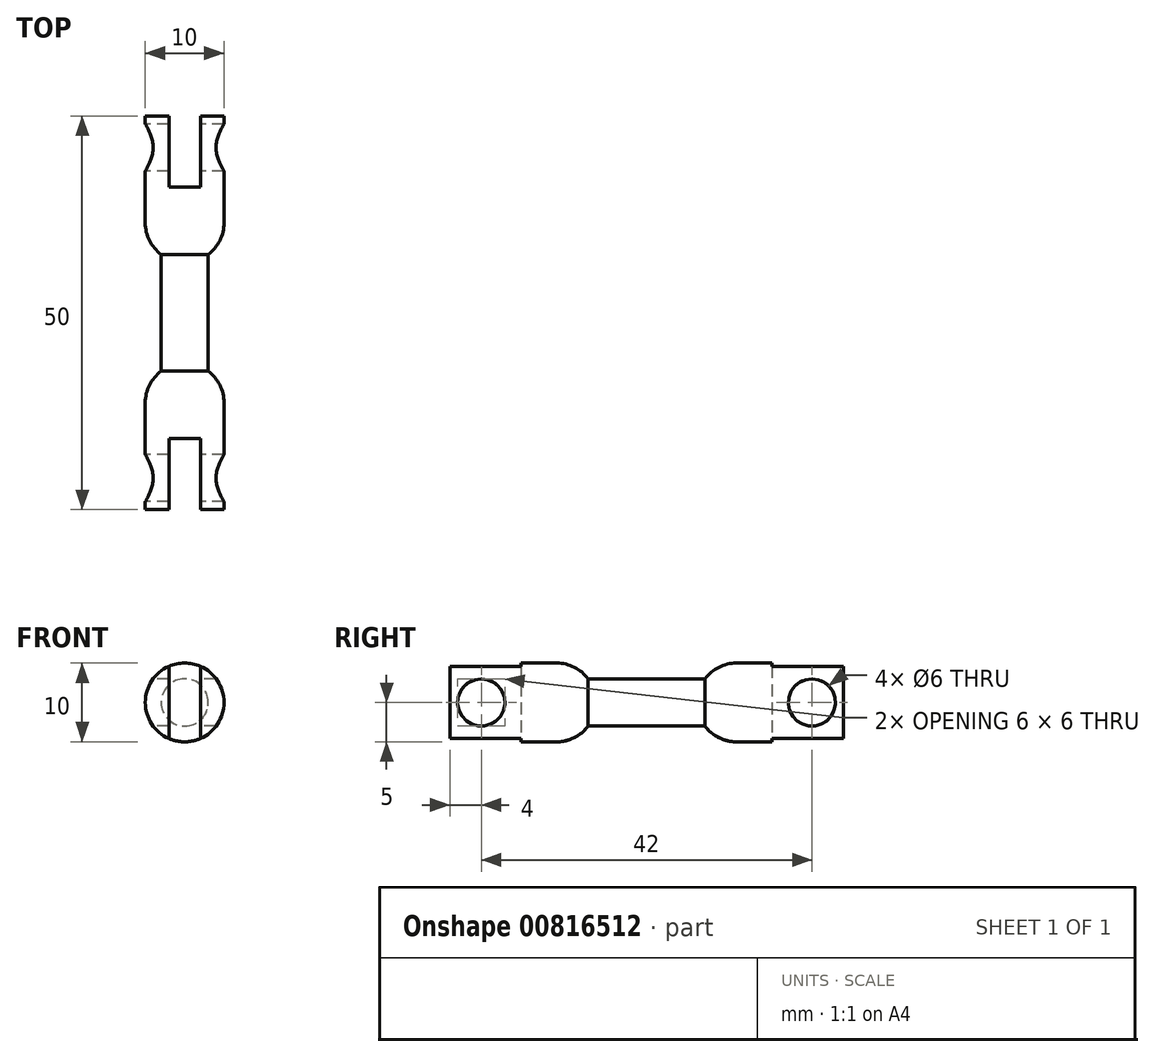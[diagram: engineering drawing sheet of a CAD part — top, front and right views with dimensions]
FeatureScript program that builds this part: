
annotation { "Feature Type Name" : "Feature", "Feature Type Description" : "" }
export const myFeature = defineFeature(function(context is Context, id is Id, definition is map)
    precondition{}
    {
        {
            assignVariable(context, id + "F0", {"name" : "Bolzenlaenge", "anyValue" : 15});
        }
        {
            var Q0;
            Q0=qCreatedBy(makeId("Front.planeOp"),FACE);
            var sketch = newSketch(context, id + "F1", { "sketchPlane" : qUnion([Q0])});
            skCircle(sketch, "E0", {"center": v(0, 0) * mm, "radius": 3 * mm});
            skCircle(sketch, "E1", {"center": v(0, 0) * mm, "radius": 5 * mm});
            skSolve(sketch);
        }
        {
            var Q0;
            Q0=makeQuery(id+"F1.imprint","IMPRINT",FACE,{"disambiguationData":[TD([[makeQuery(id+"F1.imprint","IMPRINT",EDGE,{"derivedFrom":sQuery(id+"F1.wireOp",EDGE,"E0")}),1.0]])]});
            var Q1;
            Q1=sQuery(id+"F1.wireOp",EDGE,"E0");
            extrude(context, id + "F2", {"entities" : qUnion([Q0]), "surfaceEntities" : qUnion([Q1]), "depth" : (getVariable(context, 'Bolzenlaenge')) * mm, "offsetDistance" : 25 * mm});
        }
        {
            var Q0;
            Q0=makeQuery(id+"F1.imprint","IMPRINT",FACE,{"disambiguationData":[TD([[makeQuery(id+"F1.imprint","IMPRINT",EDGE,{"derivedFrom":sQuery(id+"F1.wireOp",EDGE,"E0")}),-1.0]])]});
            var Q1;
            Q1=makeQuery(id+"F1.imprint","IMPRINT",FACE,{"disambiguationData":[TD([[makeQuery(id+"F1.imprint","IMPRINT",EDGE,{"derivedFrom":sQuery(id+"F1.wireOp",EDGE,"E0")}),1.0]])]});
            extrude(context, id + "F3", {"entities" : qUnion([Q0, Q1]), "oppositeDirection" : true, "depth" : 10 * mm, "offsetDistance" : 25 * mm, "hasSecondDirection" : true, "secondDirectionOppositeDirection" : false, "secondDirectionDepth" : 8.58 * mm});
        }
        {
            var Q0;
            Q0=makeQuery(id+"F3.opExtrude","CAP_EDGE",EDGE,{"disambiguationData":[OSD([sQuery(id+"F1.wireOp",EDGE,"E1")])],"isStart":true});
            fillet(context, id + "F4", {"entities" : qUnion([Q0]), "radius" : 5 * mm, "tangentPropagation" : true, "allowEdgeOverflow" : false});
        }
        {
            var Q0;
            Q0=makeQuery(id+"F3.opExtrude","CAP_FACE",FACE,{"disambiguationData":[OSD([sQuery(id+"F1.wireOp",EDGE,"E1")])],"isStart":false});
            var sketch = newSketch(context, id + "F5", { "sketchPlane" : qUnion([Q0])});
            skArc(sketch, "E2", {"start": v(-2, -4.58) * mm, "mid": v(0, -5) * mm, "end": v(2, -4.58) * mm});
            skLineSegment(sketch, "E3", {"start": v(-2, 4.58) * mm, "end": v(-2, -4.58) * mm});
            skLineSegment(sketch, "E4.MirrorCS", {"start": v(2, 4.58) * mm, "end": v(2, -4.58) * mm});
            skPoint(sketch, "E5.orphan", {"position": v(-2, 5.32) * mm});
            skPoint(sketch, "E6.orphan", {"position": v(-2, -6.45) * mm});
            skPoint(sketch, "E7.orphan", {"position": v(2, -6.45) * mm});
            skArc(sketch, "E8.trimOffspring", {"start": v(2, 4.58) * mm, "mid": v(0, 5) * mm, "end": v(-2, 4.58) * mm});
            skPoint(sketch, "E9.orphan", {"position": v(2, 5.32) * mm});
            skSolve(sketch);
        }
        {
            var Q0;
            Q0=makeQuery(id+"F5.imprint","IMPRINT",FACE,{"disambiguationData":[TD([[makeQuery(id+"F5.imprint","IMPRINT",EDGE,{"derivedFrom":sQuery(id+"F5.wireOp",EDGE,"E2")}),-1.0]])]});
            extrude(context, id + "F6", {"entities" : qUnion([Q0]), "operationType" : NewBodyOperationType.REMOVE, "oppositeDirection" : true, "depth" : 9.05 * mm, "offsetDistance" : 25 * mm});
        }
        {
            var Q0;
            Q0=makeQuery(id+"F6.boolean.opBoolean","COPY",FACE,{"derivedFrom":makeQuery(id+"F6.opExtrude","SWEPT_FACE",FACE,{"disambiguationData":[OSD([sQuery(id+"F5.wireOp",EDGE,"E4.MirrorCS")])]})});
            var sketch = newSketch(context, id + "F7", { "sketchPlane" : qUnion([Q0])});
            skCircle(sketch, "E10", {"center": v(6, 0) * mm, "radius": 3 * mm});
            skSolve(sketch);
        }
        {
            var Q0;
            {var subQ0=sQuery(id+"F7.wireOp",EDGE,"E10");var subQ1=makeQuery(id+"F6.boolean.opBoolean","COPY",EDGE,{"derivedFrom":makeQuery(id+"F6.opExtrude","CAP_EDGE",EDGE,{"disambiguationData":[OSD([sQuery(id+"F5.wireOp",EDGE,"E4.MirrorCS")])],"isStart":false})});var subQ2=makeQuery(id+"F7.imprint","INTERSECT",VERTEX,{"disambiguationData":[OD(0.0)],"derivedFrom":[subQ1,subQ0]});Q0=makeQuery(id+"F7.imprint","IMPRINT",FACE,{"disambiguationData":[TD([[makeQuery(id+"F7.imprint","IMPRINT",EDGE,{"disambiguationData":[TD([[subQ2,-1.0]])],"derivedFrom":subQ0}),1.0]])]});}
            extrude(context, id + "F8", {"entities" : qUnion([Q0]), "operationType" : NewBodyOperationType.REMOVE, "depth" : 25 * mm, "offsetDistance" : 25 * mm, "hasSecondDirection" : true, "secondDirectionOppositeDirection" : true, "secondDirectionDepth" : 25 * mm});
        }
        {
            var Q0;
            Q0=makeQuery(id+"F2.opExtrude","SWEPT_BODY",BODY,{"disambiguationData":[OSD([sQuery(id+"F1.wireOp",EDGE,"E0")])]});
            var Q1;
            Q1=makeQuery(id+"F3.opExtrude","SWEPT_BODY",BODY,{"disambiguationData":[OSD([sQuery(id+"F1.wireOp",EDGE,"E1")])]});
            var Q2;
            Q2=makeQuery(id+"F2.opExtrude","CAP_FACE",FACE,{"disambiguationData":[OSD([sQuery(id+"F1.wireOp",EDGE,"E0")])],"isStart":false});
            mirror(context, id + "F9", {"operationType" : NewBodyOperationType.ADD, "entities" : qUnion([Q0, Q1]), "mirrorPlane" : qUnion([Q2])});
        }
    });
